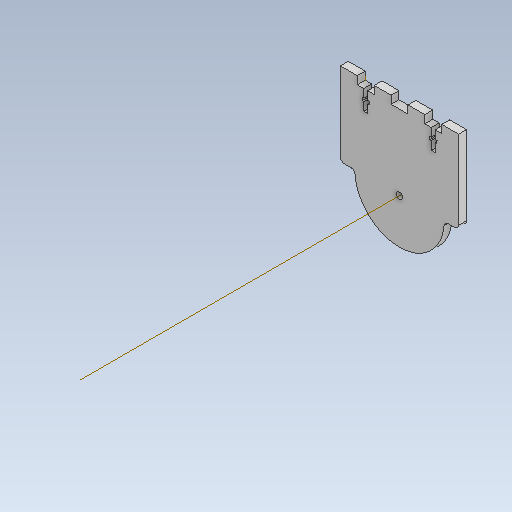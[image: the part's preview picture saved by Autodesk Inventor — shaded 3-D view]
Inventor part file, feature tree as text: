
AUTODESK INVENTOR PART (.ipt)
format: ipt  version: 2021.1 (Build 251245010, 245A)  size: 175,616 bytes
history: native  units: mm
features: other x8, reference x6, extrude x2, sketch x1
ambient origin geometry x8: Origin, YZ Plane, XZ Plane, XY Plane, X Axis, Y Axis, Z Axis, Center Point
bodies: Body1 (feature_tree)
feature tree (17):
  other  "Твердое тело1"
  other  "РабПлоскость1"
  other  "РабОсь1"
  extrude  "Выдавливание1"  Depth=57.0mm
  extrude  "Выдавливание2"  Depth=34.0mm
  reference  "Ссылка1"
  reference  "Ссылка2"
  reference  "Ссылка3"
  reference  "Ссылка4"
  other  "РабПлоскость2"
  sketch  "Эскиз2"
  reference  "Ссылка8"
  reference  "Ссылка9"
  other  "<userpath>\Documents\Savka\3d\Korp.iam"
  other  "Korp.iam"
  other  "Korpus 3:1"
  other  "Korpus:1"
